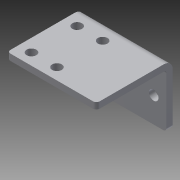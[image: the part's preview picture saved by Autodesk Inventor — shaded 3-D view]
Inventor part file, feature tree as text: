
AUTODESK INVENTOR PART (.ipt)
format: ipt  version: 2014 (Build 180170000, 170)  size: 201,216 bytes
history: native  units: in
note: dims shown in document units (in); Inventor stores cm internally (conversion verified against a paired STEP export)
features: sheet_metal_op x4, other x4, sketch x3, fillet x1, extrude x1
ambient origin geometry x8: Origin, YZ Plane, XZ Plane, XY Plane, X Axis, Y Axis, Z Axis, Center Point
bodies: Solid1 (feature_tree)
feature tree (13):
  sheet_metal_op  "Face1"
  sheet_metal_op  "Flange1"
  fillet  "Fillet1"  Radius=1.75in
  extrude  "Extrusion1"  Depth=0.19in
  sketch  "Sketch1"  dims[d1=1.0in d2=0.19in]
  other  "Plate1"
  sketch  "Sketch2"  dims[d4=0.7874in d6=1.0in d7=0.3937in d9=1.0in]
  other  "Plate2"
  sheet_metal_op  "Bend1"
  sheet_metal_op  "Corner1"
  sketch  "Sketch3"  dims[d11=0.125in d12=0.125in d13=0.0625in d14=0.25in d15=0.125in d16=1.5in d17=90.0deg d18=0.05in d19=0.5in d20=0.125in d21=0.125in d22=0.0625in d23=1.35in d24=0.75in d27=0.19in d28=0.125in d29=0.2265in d30=1.0in d31=0.0in d32=0.25in d33=0.875in d3=0.0in d5=0.0625in d8=0.0625in]
  other  "Definition1"
  other  "Cut1"
